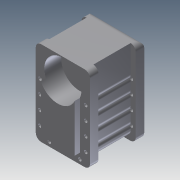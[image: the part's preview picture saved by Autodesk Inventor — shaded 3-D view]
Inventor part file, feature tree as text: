
AUTODESK INVENTOR PART (.ipt)
format: ipt  version: 2011 (Build 150239000, 239)  size: 265,728 bytes
history: native  units: in
note: dims shown in document units (in); Inventor stores cm internally (conversion verified against a paired STEP export)
features: extrude x8, sketch x8, fillet x3
ambient origin geometry x8: Origin, YZ Plane, XZ Plane, XY Plane, X Axis, Y Axis, Z Axis, Center Point
bodies: Solid1 (feature_tree)
feature tree (19):
  extrude  "Extrusion1"  Depth=1.9685in
  extrude  "Extrusion2"  Depth=0.4528in
  extrude  "Extrusion3"  Depth=0.3937in TaperAngle=0.0deg
  extrude  "Extrusion4"  Depth=0.7874in
  extrude  "Extrusion5"  Depth=0.5118in
  extrude  "Extrusion6"  Depth=0.1969in
  fillet  "Fillet1"  Radius=0.1969in
  fillet  "Fillet2"  Radius=0.1969in
  extrude  "Extrusion7"  Depth=0.1969in
  extrude  "Extrusion8"  Depth=0.1969in
  fillet  "Fillet3"  Radius=0.1969in
  sketch  "Sketch1"  dims[d0=1.2598in d1=1.9685in]
  sketch  "Sketch2"  dims[d2=1.2598in d3=0.0in d4=0.4528in]
  sketch  "Sketch3"  dims[d5=0.8661in d6=0.3937in d7=0.0in]
  sketch  "Sketch4"  dims[d8=1.1024in d9=0.7874in]
  sketch  "Sketch5"  dims[d10=0.1181in d11=0.0in d12=0.5118in]
  sketch  "Sketch6"  dims[d13=1.0236in d14=0.1969in d15=0.1969in d16=0.1969in]
  sketch  "Sketch7"  dims[d17=50.0in d18=0.0in d19=0.1969in]
  sketch  "Sketch8"  dims[d20=0.1969in d21=0.1969in d22=0.1969in d23=0.1181in d24=0.0in d25=0.4528in d26=0.2559in d27=0.315in d28=0.315in d29=0.315in d30=0.0984in d31=0.0984in d32=0.0787in d33=3.0in d34=0.0in d35=0.125in d36=0.125in d37=0.1181in d38=3.0in d39=0.0in d40=0.315in d41=0.0984in d42=0.7087in d43=0.0787in d44=0.0787in d45=3.0in d46=0.0in d47=0.125in]
